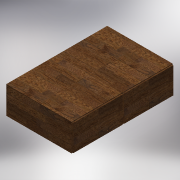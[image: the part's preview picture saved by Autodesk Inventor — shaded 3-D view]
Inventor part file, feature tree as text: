
AUTODESK INVENTOR PART (.ipt)
format: ipt  version: 2016 (Build 200138000, 138)  size: 524,288 bytes
history: native  units: mm
features: extrude x4, sketch x4, projected_geometry x2, other x1, plane x1
ambient origin geometry x8: Origin, YZ Plane, XZ Plane, XY Plane, X Axis, Y Axis, Z Axis, Center Point
bodies: Body1 (feature_tree)
feature tree (12):
  other  "Sólido3"
  plane  "Plano de trabajo1"
  extrude  "Extrusión1"  Depth=10.0mm
  extrude  "Extrusión2"  Depth=10.0mm
  extrude  "Extrusión3"  Depth=5.0mm
  extrude  "Extrusión4"  Depth=5.0mm
  sketch  "Boceto1"  dims[d1=0.0mm d3=10.0mm]
  sketch  "Boceto2"  dims[d4=10.0mm d5=10.0mm]
  sketch  "Boceto3"  dims[d6=545.0mm d7=0.0mm d8=5.0mm]
  sketch  "Boceto4"  dims[d9=5.0mm d10=5.0mm d11=5.0mm d12=10.0mm d13=0.0mm d15=30.2519mm d16=80.0mm d17=80.0mm d18=6.0mm d19=50.0mm d20=6.0mm d21=50.0mm d22=10.0mm d23=0.0mm]
  projected_geometry  "Contorno proyectado1"
  projected_geometry  "Contorno proyectado2"
